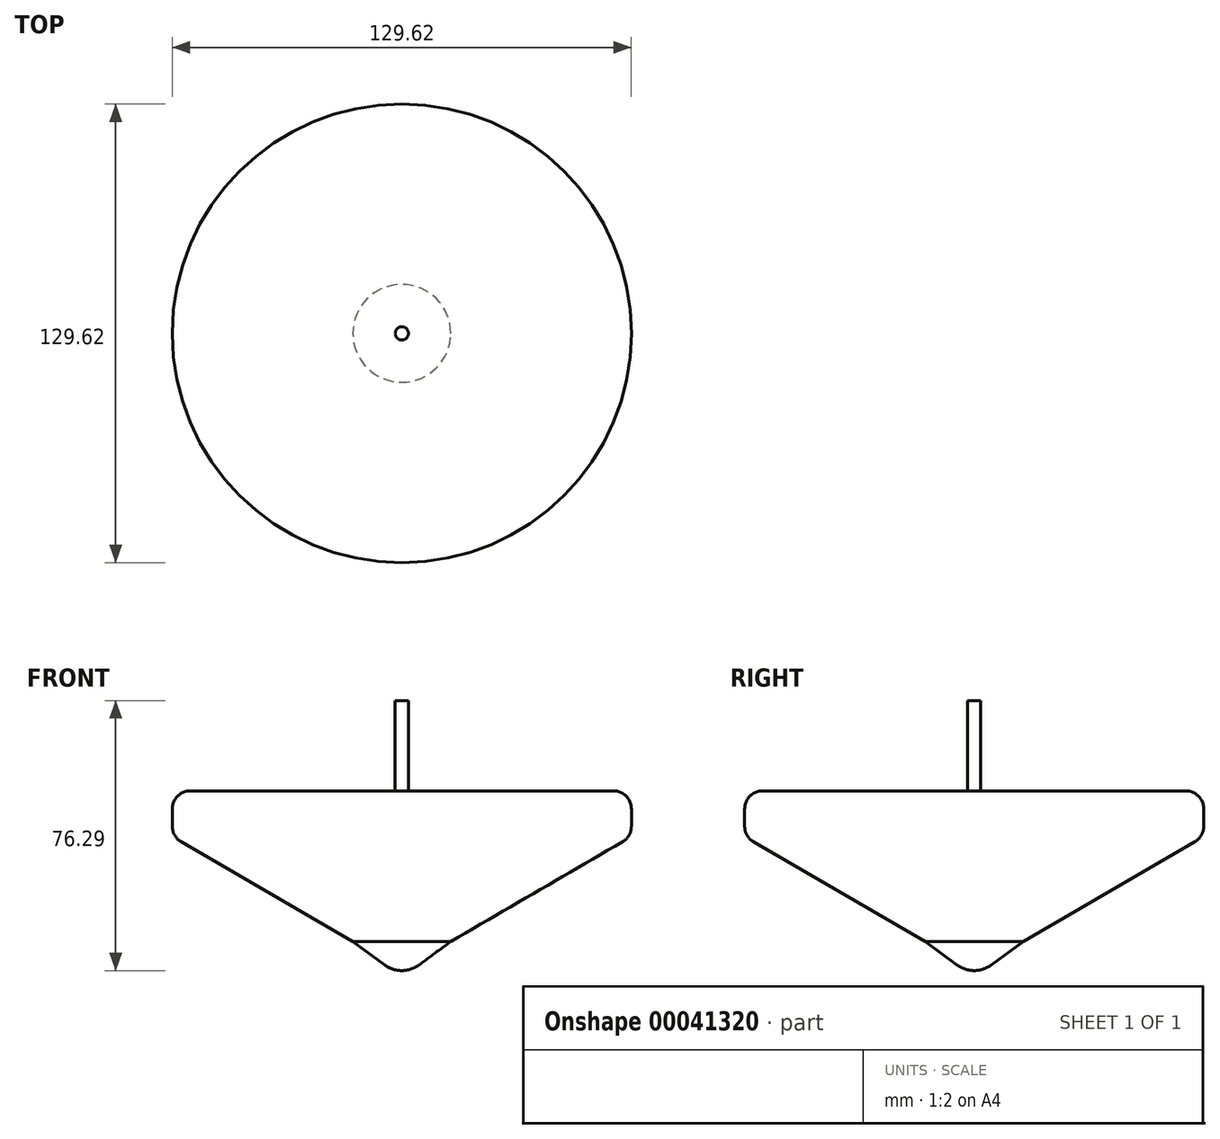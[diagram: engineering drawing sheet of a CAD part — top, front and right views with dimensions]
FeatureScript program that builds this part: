
annotation { "Feature Type Name" : "Feature", "Feature Type Description" : "" }
export const myFeature = defineFeature(function(context is Context, id is Id, definition is map)
    precondition{}
    {
        {
            var Q0;
            Q0=qCreatedBy(makeId("Front.planeOp"),FACE);
            var sketch = newSketch(context, id + "F0", { "sketchPlane" : qUnion([Q0])});
            skLineSegment(sketch, "E0", {"start": v(13.83, 0) * mm, "end": v(64.81, 29.61) * mm});
            skLineSegment(sketch, "E1", {"start": v(64.81, 29.61) * mm, "end": v(64.81, 42.57) * mm});
            skLineSegment(sketch, "E2", {"start": v(64.81, 42.57) * mm, "end": v(1.86, 42.57) * mm});
            skLineSegment(sketch, "E3", {"start": v(1.86, 42.57) * mm, "end": v(1.86, 68.06) * mm});
            skLineSegment(sketch, "E4", {"start": v(1.86, 68.06) * mm, "end": v(0, 68.06) * mm});
            skLineSegment(sketch, "E5", {"start": v(0, 68.06) * mm, "end": v(0, -8.23) * mm});
            skLineSegment(sketch, "E6", {"start": v(13.83, 0) * mm, "end": v(4.9, -6.62) * mm});
            skArc(sketch, "E7", {"start": v(-4.9, -6.62) * mm, "mid": v(0, -8.23) * mm, "end": v(4.9, -6.62) * mm});
            skSolve(sketch);
        }
        {
            var Q0;
            Q0 = qSketchRegion(id + "F0", true);
            var Q1;
            Q1=sQuery(id+"F0.wireOp",EDGE,"E5");
            revolve(context, id + "F1", {"entities" : qUnion([Q0]), "axis" : qUnion([Q1]), "revolveType" : RevolveType.FULL});
        }
        {
            var Q0;
            Q0=makeQuery(id+"F1.opRevolve","SWEPT_EDGE",EDGE,{"disambiguationData":[OSD([sQuery(id+"F0.wireOp",EDGE,"E1"),sQuery(id+"F0.wireOp",EDGE,"E2")])]});
            var Q1;
            Q1=makeQuery(id+"F1.opRevolve","SWEPT_EDGE",EDGE,{"disambiguationData":[OSD([sQuery(id+"F0.wireOp",EDGE,"E0"),sQuery(id+"F0.wireOp",EDGE,"E1")])]});
            fillet(context, id + "F2", {"entities" : qUnion([Q0, Q1]), "radius" : 5.08 * mm, "tangentPropagation" : true, "allowEdgeOverflow" : false});
        }
    });
